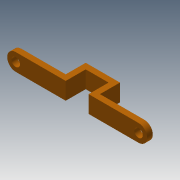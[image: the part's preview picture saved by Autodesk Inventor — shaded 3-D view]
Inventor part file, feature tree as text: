
AUTODESK INVENTOR PART (.ipt)
format: ipt  version: 2013 (Build 170138000, 138)  size: 126,464 bytes
history: native  units: mm
features: sketch x8, extrude x7
ambient origin geometry x8: Origin, YZ Plane, XZ Plane, XY Plane, X Axis, Y Axis, Z Axis, Center Point
bodies: Solid1 (feature_tree)
feature tree (15):
  sketch  "Sketch1"  dims[d6=43.0mm d7=6.0mm]
  extrude  "Extrusion1"  Depth=6.0mm
  extrude  "Extrusion2"  Depth=10.0mm
  extrude  "Extrusion3"  Depth=8.0mm
  extrude  "Extrusion4"  Depth=1.0mm TaperAngle=0.0deg
  extrude  "Extrusion5"  Depth=3.0mm
  sketch  "Sketch7"  dims[d24=2.0mm d25=0.0mm]
  extrude  "Extrusion6"  Depth=2.0mm TaperAngle=0.0deg
  extrude  "Extrusion7"  [1 undecoded]
  sketch  "Sketch2"  dims[d8=2.0mm d9=0.0mm d10=10.0mm]
  sketch  "Sketch3"  dims[d11=7.0mm d12=0.0mm d13=8.0mm]
  sketch  "Sketch4"  dims[d14=7.0mm d15=0.0mm d16=1.0mm d17=0.0mm]
  sketch  "Sketch5"  dims[d18=1.0mm d19=0.0mm d20=3.0mm]
  sketch  "Sketch6"  dims[d21=3.0mm d22=2.0mm d23=0.0mm]
  sketch  "Sketch8"
note: 1 required parameter value undecoded (feature->parameter linkage not recoverable at this tier; creation-order binding heuristic only, values carry confidence <= 0.55)
